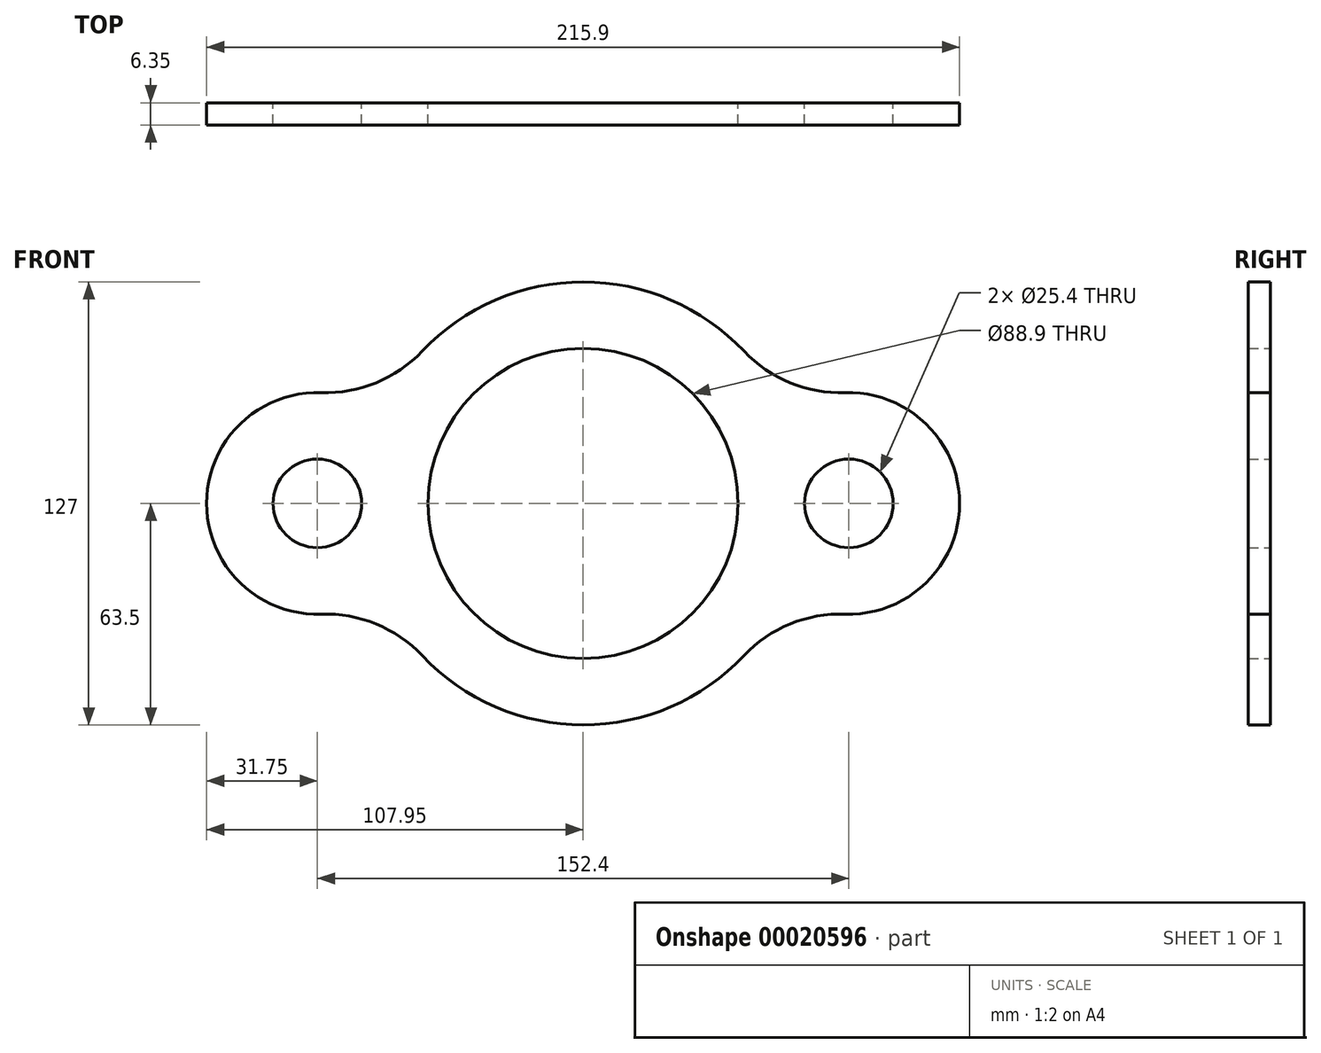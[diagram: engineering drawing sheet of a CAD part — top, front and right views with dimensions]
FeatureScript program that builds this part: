
annotation { "Feature Type Name" : "Feature", "Feature Type Description" : "" }
export const myFeature = defineFeature(function(context is Context, id is Id, definition is map)
    precondition{}
    {
        {
            var Q0;
            Q0=qCreatedBy(makeId("Front.planeOp"),FACE);
            var sketch = newSketch(context, id + "F0", { "sketchPlane" : qUnion([Q0])});
            skCircle(sketch, "E0", {"center": v(0, 0) * mm, "radius": 44.45 * mm});
            skArc(sketch, "E1", {"start": v(-46.14, -43.63) * mm, "mid": v(0, -63.5) * mm, "end": v(46.14, -43.63) * mm});
            skCircle(sketch, "E2", {"center": v(-76.2, 0) * mm, "radius": 12.7 * mm});
            skCircle(sketch, "E3", {"center": v(76.2, 0) * mm, "radius": 12.7 * mm});
            skArc(sketch, "E4", {"start": v(-75.12, 31.73) * mm, "mid": v(-107.95, 0) * mm, "end": v(-75.12, -31.73) * mm});
            skArc(sketch, "E5", {"start": v(75.12, -31.73) * mm, "mid": v(107.95, 0) * mm, "end": v(75.12, 31.73) * mm});
            skArc(sketch, "E6.trimOffspring", {"start": v(46.14, 43.63) * mm, "mid": v(0, 63.5) * mm, "end": v(-46.14, 43.63) * mm});
            skPoint(sketch, "E7.visualSharp", {"position": v(-57.94, 25.98) * mm});
            skArc(sketch, "E7.filletArc", {"start": v(-75.12, 31.73) * mm, "mid": v(-59.35, 34.56) * mm, "end": v(-46.14, 43.63) * mm});
            skPoint(sketch, "E8.visualSharp", {"position": v(-57.94, -25.98) * mm});
            skArc(sketch, "E8.filletArc", {"start": v(-46.14, -43.63) * mm, "mid": v(-59.35, -34.56) * mm, "end": v(-75.12, -31.73) * mm});
            skPoint(sketch, "E9.visualSharp", {"position": v(57.94, 25.98) * mm});
            skArc(sketch, "E9.filletArc", {"start": v(46.14, 43.63) * mm, "mid": v(59.35, 34.56) * mm, "end": v(75.12, 31.73) * mm});
            skPoint(sketch, "E10.visualSharp", {"position": v(57.94, -25.98) * mm});
            skArc(sketch, "E10.filletArc", {"start": v(75.12, -31.73) * mm, "mid": v(59.35, -34.56) * mm, "end": v(46.14, -43.63) * mm});
            skSolve(sketch);
        }
        {
            var Q0;
            Q0 = qSketchRegion(id + "F0", true);
            extrude(context, id + "F1", {"entities" : qUnion([Q0]), "depth" : 6.35 * mm});
        }
    });
